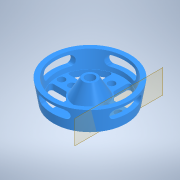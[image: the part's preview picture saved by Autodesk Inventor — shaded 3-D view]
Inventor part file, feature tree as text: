
AUTODESK INVENTOR PART (.ipt)
format: ipt  version: 2022 (Build 260153000, 153)  size: 297,984 bytes
history: native  units: in
note: dims shown in document units (in); Inventor stores cm internally (conversion verified against a paired STEP export)
features: sketch x3, extrude x2, revolve x1, plane x1, pattern_circular x1, fillet x1
ambient origin geometry x8: Origin, YZ Plane, XZ Plane, XY Plane, X Axis, Y Axis, Z Axis, Center Point
bodies: Solid1 (feature_tree)
feature tree (9):
  revolve  "Revolution1"  [1 undecoded]
  plane  "Work Plane1"
  extrude  "Extrusion1"  TaperAngle=360.0deg  [1 undecoded]
  pattern_circular  "Circular Pattern1"  [2 undecoded]
  extrude  "Extrusion2"  Depth=0.1673in
  fillet  "Fillet1"  Radius=1.384in
  sketch  "Sketch1"  dims[d0=0.6919in d1=0.374in]
  sketch  "Sketch2"  dims[d2=0.6299in d3=360.0deg]
  sketch  "Sketch3"  dims[d4=0.1969in d5=0.1575in d6=0.1673in d7=1.384in d8=0.0in d9=1.5748in d10=360.0deg d12=0.0787in d13=0.0984in d14=0.1969in d15=0.1575in d16=0.0787in d18=0.1181in d19=0.2756in d20=0.5in d21=0.748in d22=0.6299in d23=0.9843in d24=0.1181in d25=0.1181in d26=0.1181in d27=0.5906in d28=1.122in d29=0.1378in d30=0.1378in d31=0.1378in d32=0.1378in d33=0.2953in d34=0.7874in d36=360.0deg d38=1.5748in d40=360.0deg d42=0.0in d43=0.0in d44=0.0394in]
note: 4 required parameter values undecoded (feature->parameter linkage not recoverable at this tier; creation-order binding heuristic only, values carry confidence <= 0.55)